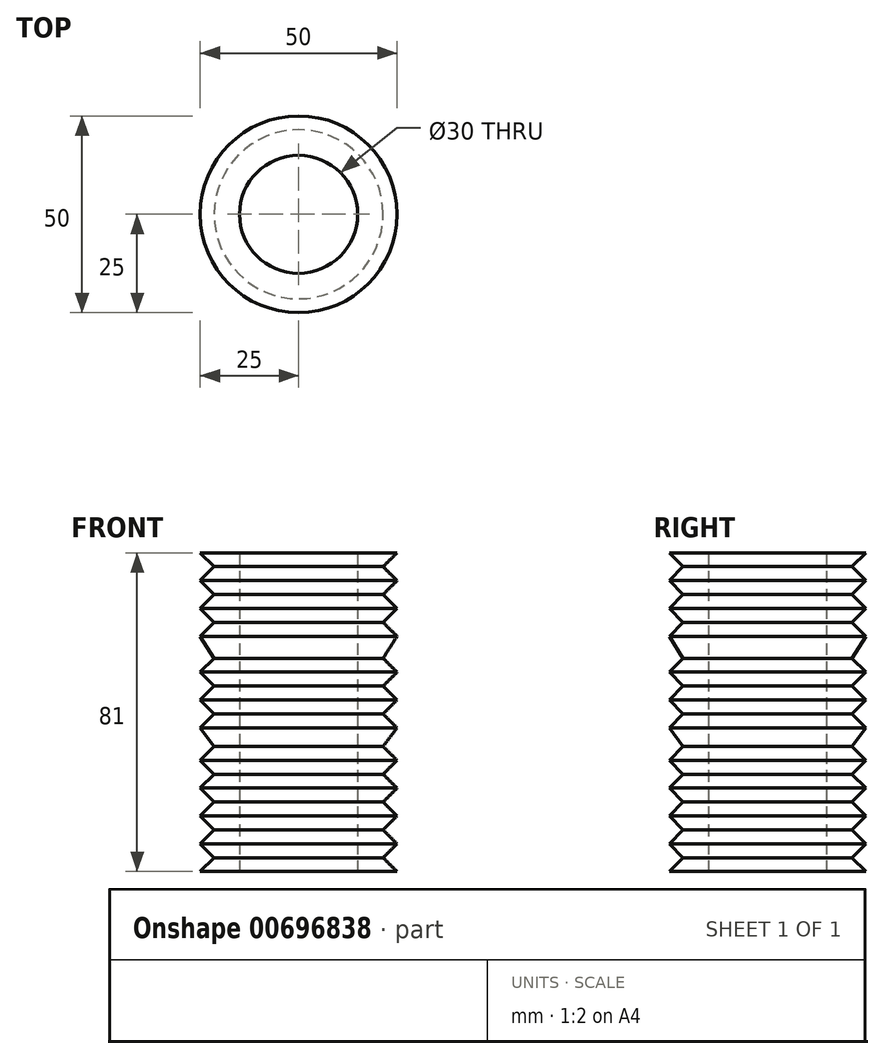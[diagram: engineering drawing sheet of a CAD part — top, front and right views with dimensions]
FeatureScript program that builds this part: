
annotation { "Feature Type Name" : "Feature", "Feature Type Description" : "" }
export const myFeature = defineFeature(function(context is Context, id is Id, definition is map)
    precondition{}
    {
        {
            var Q0;
            Q0=qCreatedBy(makeId("Front.planeOp"),FACE);
            var sketch = newSketch(context, id + "F0", { "sketchPlane" : qUnion([Q0])});
            skLineSegment(sketch, "E0", {"start": v(0, 64.07) * mm, "end": v(-25, 64.07) * mm});
            skLineSegment(sketch, "E1", {"start": v(-25, 64.07) * mm, "end": v(-21.46, 60.53) * mm});
            skLineSegment(sketch, "E2", {"start": v(-21.46, 60.53) * mm, "end": v(-25, 57) * mm});
            skLineSegment(sketch, "E3", {"start": v(-25, 57) * mm, "end": v(-21.46, 53.46) * mm});
            skLineSegment(sketch, "E4", {"start": v(-21.46, 53.46) * mm, "end": v(-25, 49.93) * mm});
            skLineSegment(sketch, "E5", {"start": v(-25, 49.93) * mm, "end": v(-21.46, 46.4) * mm});
            skLineSegment(sketch, "E6", {"start": v(-21.46, 46.4) * mm, "end": v(-25, 42.86) * mm});
            skLineSegment(sketch, "E7", {"start": v(-21.46, 37.27) * mm, "end": v(-25, 33.74) * mm});
            skLineSegment(sketch, "E8", {"start": v(-25, 33.74) * mm, "end": v(-21.46, 30.2) * mm});
            skLineSegment(sketch, "E9", {"start": v(-21.46, 30.2) * mm, "end": v(-25, 26.67) * mm});
            skLineSegment(sketch, "E10", {"start": v(-25, 26.67) * mm, "end": v(-21.46, 23.13) * mm});
            skLineSegment(sketch, "E11", {"start": v(-21.46, 23.13) * mm, "end": v(-25, 19.6) * mm});
            skLineSegment(sketch, "E12", {"start": v(-21.46, 37.27) * mm, "end": v(-25, 42.86) * mm});
            skLineSegment(sketch, "E13", {"start": v(0, 64.07) * mm, "end": v(0, -16.93) * mm});
            skLineSegment(sketch, "E14", {"start": v(0, -16.93) * mm, "end": v(-25, -16.93) * mm});
            skLineSegment(sketch, "E15", {"start": v(-25, -16.93) * mm, "end": v(-21.46, -13.4) * mm});
            skLineSegment(sketch, "E16", {"start": v(-21.46, -13.4) * mm, "end": v(-25, -9.86) * mm});
            skLineSegment(sketch, "E17", {"start": v(-25, -9.86) * mm, "end": v(-21.46, -6.32) * mm});
            skLineSegment(sketch, "E18", {"start": v(-21.46, -6.32) * mm, "end": v(-25, -2.79) * mm});
            skLineSegment(sketch, "E19", {"start": v(-25, -2.79) * mm, "end": v(-21.46, 0.75) * mm});
            skLineSegment(sketch, "E20", {"start": v(-21.46, 0.75) * mm, "end": v(-25, 4.28) * mm});
            skLineSegment(sketch, "E21", {"start": v(-25, 4.28) * mm, "end": v(-21.46, 7.82) * mm});
            skLineSegment(sketch, "E22", {"start": v(-21.46, 7.82) * mm, "end": v(-25, 11.35) * mm});
            skLineSegment(sketch, "E23", {"start": v(-25, 11.35) * mm, "end": v(-21.46, 14.89) * mm});
            skLineSegment(sketch, "E24", {"start": v(-21.46, 14.89) * mm, "end": v(-25, 19.6) * mm});
            skSolve(sketch);
        }
        {
            var Q0;
            Q0 = qSketchRegion(id + "F0", true);
            var Q1;
            Q1=sQuery(id+"F0.wireOp",EDGE,"E13");
            revolve(context, id + "F1", {"entities" : qUnion([Q0]), "axis" : qUnion([Q1]), "revolveType" : RevolveType.FULL});
        }
        {
            var Q0;
            Q0=makeQuery(id+"F1.opRevolve","SWEPT_FACE",FACE,{"disambiguationData":[OSD([sQuery(id+"F0.wireOp",EDGE,"E14")])]});
            var sketch = newSketch(context, id + "F2", { "sketchPlane" : qUnion([Q0])});
            skCircle(sketch, "E25", {"center": v(0, 0) * mm, "radius": 15 * mm});
            skSolve(sketch);
        }
        {
            var Q0;
            Q0=makeQuery(id+"F2.imprint","IMPRINT",FACE,{"disambiguationData":[TD([[makeQuery(id+"F2.imprint","IMPRINT",EDGE,{"derivedFrom":sQuery(id+"F2.wireOp",EDGE,"E25")}),1.0]])]});
            extrude(context, id + "F3", {"entities" : qUnion([Q0]), "operationType" : NewBodyOperationType.REMOVE, "endBound" : BoundingType.THROUGH_ALL, "oppositeDirection" : true, "depth" : 25 * mm, "offsetDistance" : 25 * mm});
        }
    });
